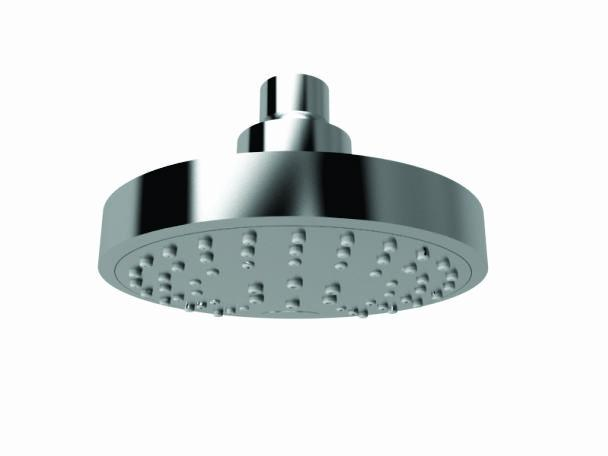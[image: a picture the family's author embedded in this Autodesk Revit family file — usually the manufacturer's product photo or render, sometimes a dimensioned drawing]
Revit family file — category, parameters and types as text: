
# Revit family: Regadera H-3300
name_source: partatom
category: Aparatos sanitarios
revit_build: Autodesk Revit 2016 (Build: 20150220_1215(x64)
units: mm (PartAtom-declared; Revit-internal decimal feet)

## family parameters
Anfitrión = Cara
Compartido = Sí
Corte con vacíos al cargar = No
Cota de conector redondo = Diámetro de uso
Número OmniClass = 23.45.05.14.17
Punto de cálculo de habitación = Sí
Tipo de pieza = Normal
Título OmniClass = Showers

## types (1)
- Regadera H-3300
    Comentarios de tipo = Regadera redonda de plato ancho multichorro 5"
3 Chorros.
    Conexión = ½"-14 NPSM
    Descripción = Regadera redonda de plato ancho multichorro 5"
3 Chorros.
    Elevación por defecto = 0.5 "
    Fabricante = HELVEX S.A. DE C.V.
    Imagen de tipo = H-3300.jpg
    Material = Brass Chromed
    Modelo = H-3300
    Presión máxima de trabajo = 85.3 psi
    Presión mínima de trabajo = 14.2 psi
    Total Diameter = 4.6 "
    Total Length = 10.4 "

## geometry (parser evidence)
native form markers: Sweep x8
no freeform markers — native parametric forms only
